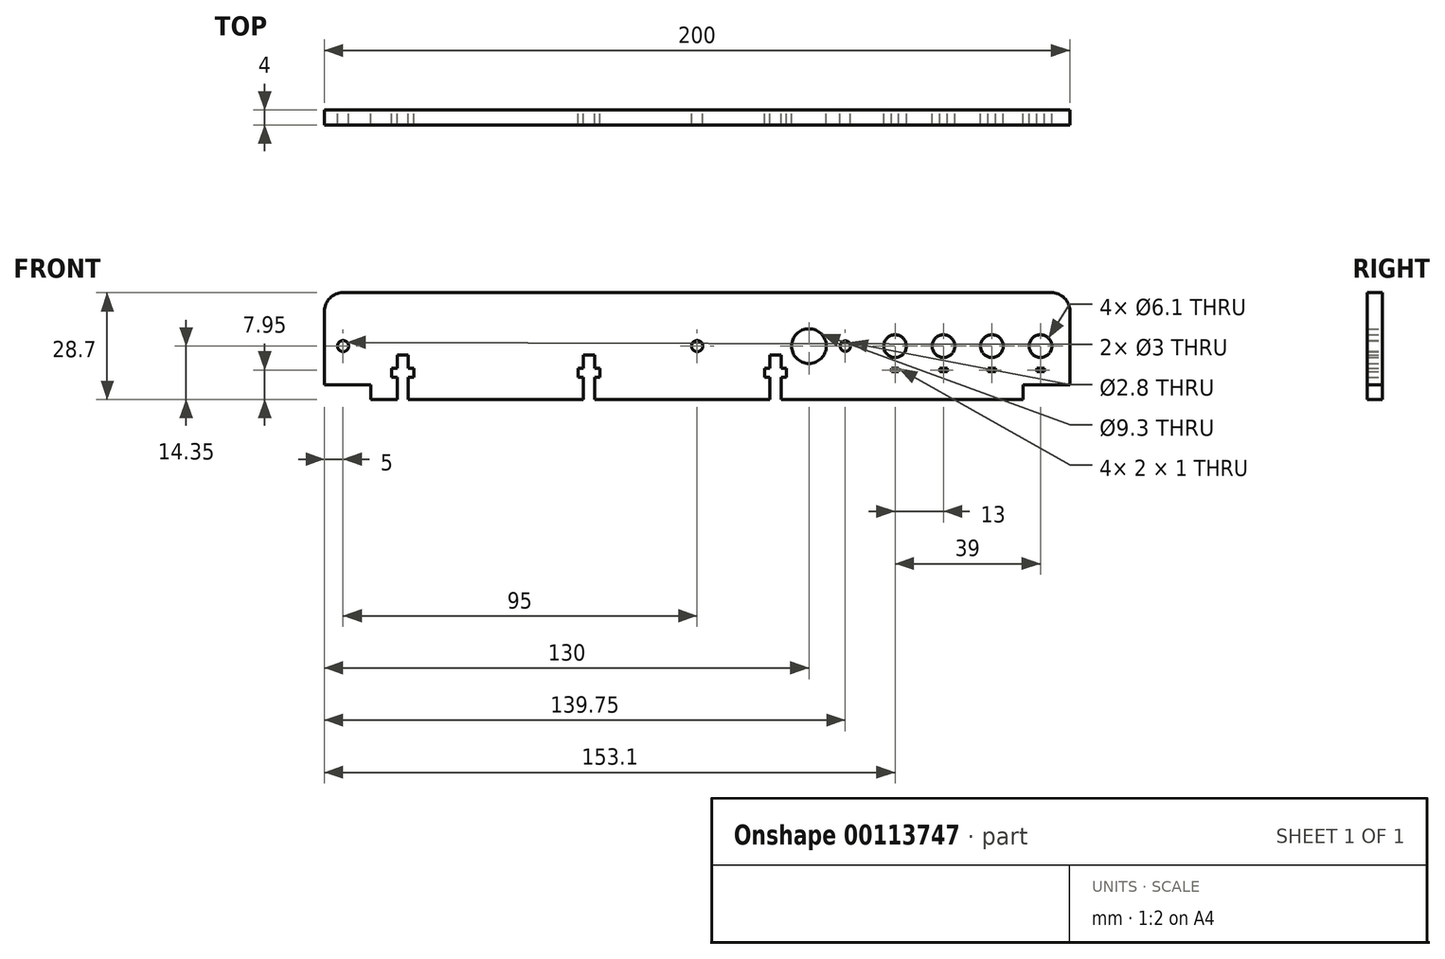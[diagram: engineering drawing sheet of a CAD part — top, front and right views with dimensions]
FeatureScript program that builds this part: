
annotation { "Feature Type Name" : "Feature", "Feature Type Description" : "" }
export const myFeature = defineFeature(function(context is Context, id is Id, definition is map)
    precondition{}
    {
        {
            var Q0;
            Q0=qCreatedBy(makeId("Front.planeOp"),FACE);
            var sketch = newSketch(context, id + "F0", { "sketchPlane" : qUnion([Q0])});
            skLineSegment(sketch, "E0.bottom", {"start": v(5, 28.7) * mm, "end": v(195, 28.7) * mm});
            skLineSegment(sketch, "E0.top", {"start": v(12.5, 0) * mm, "end": v(19.5, 0) * mm});
            skLineSegment(sketch, "E0.left", {"start": v(0, 23.7) * mm, "end": v(0, 4) * mm});
            skLineSegment(sketch, "E0.right", {"start": v(200, 23.7) * mm, "end": v(200, 4) * mm});
            skCircle(sketch, "E1", {"center": v(130, 14.35) * mm, "radius": 4.65 * mm});
            skCircle(sketch, "E2", {"center": v(139.75, 14.35) * mm, "radius": 1.4 * mm});
            skLineSegment(sketch, "E3", {"start": v(0, 14.35) * mm, "end": v(200, 14.35) * mm, "construction": true});
            skLineSegment(sketch, "E4.top", {"start": v(0, 4) * mm, "end": v(12.5, 4) * mm});
            skLineSegment(sketch, "E4.right", {"start": v(12.5, 0) * mm, "end": v(12.5, 4) * mm});
            skLineSegment(sketch, "E5", {"start": v(100, 28.7) * mm, "end": v(100, 0) * mm, "construction": true});
            skPoint(sketch, "E6.orphan", {"position": v(0, 0) * mm});
            skLineSegment(sketch, "E7.MirrorCS", {"start": v(187.5, 0) * mm, "end": v(187.5, 4) * mm});
            skLineSegment(sketch, "E8.MirrorCS", {"start": v(200, 4) * mm, "end": v(187.5, 4) * mm});
            skPoint(sketch, "E9.orphan", {"position": v(200, 0) * mm});
            skPoint(sketch, "E10.visualSharp", {"position": v(0, 28.7) * mm});
            skArc(sketch, "E10.filletArc", {"start": v(5, 28.7) * mm, "mid": v(1.46, 27.24) * mm, "end": v(0, 23.7) * mm});
            skPoint(sketch, "E11.visualSharp", {"position": v(200, 28.7) * mm});
            skArc(sketch, "E11.filletArc", {"start": v(200, 23.7) * mm, "mid": v(198.54, 27.24) * mm, "end": v(195, 28.7) * mm});
            skCircle(sketch, "E12", {"center": v(192.1, 14.35) * mm, "radius": 3.05 * mm});
            skCircle(sketch, "E13", {"center": v(192.1, 14.35) * mm, "radius": 5.9 * mm, "construction": true});
            skLineSegment(sketch, "E14", {"start": v(192.1, 14.35) * mm, "end": v(192.1, 4) * mm, "construction": true});
            skLineSegment(sketch, "E15.bottom", {"start": v(193.1, 7.45) * mm, "end": v(191.1, 7.45) * mm});
            skLineSegment(sketch, "E15.top", {"start": v(193.1, 8.45) * mm, "end": v(191.1, 8.45) * mm});
            skLineSegment(sketch, "E15.left", {"start": v(193.1, 7.45) * mm, "end": v(193.1, 8.45) * mm});
            skLineSegment(sketch, "E15.right", {"start": v(191.1, 7.45) * mm, "end": v(191.1, 8.45) * mm});
            skPoint(sketch, "E15.middle", {"position": v(192.1, 7.95) * mm});
            skCircle(sketch, "E16.1.0.0", {"center": v(179.1, 14.35) * mm, "radius": 3.05 * mm});
            skLineSegment(sketch, "E16.1.0.1", {"start": v(180.1, 7.45) * mm, "end": v(180.1, 8.45) * mm});
            skLineSegment(sketch, "E16.1.0.2", {"start": v(180.1, 8.45) * mm, "end": v(178.1, 8.45) * mm});
            skLineSegment(sketch, "E16.1.0.3", {"start": v(178.1, 7.45) * mm, "end": v(178.1, 8.45) * mm});
            skLineSegment(sketch, "E16.1.0.4", {"start": v(180.1, 7.45) * mm, "end": v(178.1, 7.45) * mm});
            skCircle(sketch, "E16.1.0.5", {"center": v(179.1, 14.35) * mm, "radius": 5.9 * mm, "construction": true});
            skCircle(sketch, "E16.2.0.0", {"center": v(166.1, 14.35) * mm, "radius": 3.05 * mm});
            skLineSegment(sketch, "E16.2.0.1", {"start": v(167.1, 7.45) * mm, "end": v(167.1, 8.45) * mm});
            skLineSegment(sketch, "E16.2.0.2", {"start": v(167.1, 8.45) * mm, "end": v(165.1, 8.45) * mm});
            skLineSegment(sketch, "E16.2.0.3", {"start": v(165.1, 7.45) * mm, "end": v(165.1, 8.45) * mm});
            skLineSegment(sketch, "E16.2.0.4", {"start": v(167.1, 7.45) * mm, "end": v(165.1, 7.45) * mm});
            skCircle(sketch, "E16.2.0.5", {"center": v(166.1, 14.35) * mm, "radius": 5.9 * mm, "construction": true});
            skLineSegment(sketch, "E16.direction1", {"start": v(191.1, 7.45) * mm, "end": v(178.1, 7.45) * mm, "construction": true});
            skLineSegment(sketch, "E17.top", {"start": v(19.5, 12) * mm, "end": v(22.5, 12) * mm});
            skLineSegment(sketch, "E17.left", {"start": v(19.5, 0) * mm, "end": v(19.5, 6) * mm});
            skLineSegment(sketch, "E17.right", {"start": v(22.5, 0) * mm, "end": v(22.5, 6) * mm});
            skCircle(sketch, "E18", {"center": v(5, 14.35) * mm, "radius": 1.5 * mm});
            skCircle(sketch, "E19", {"center": v(100, 14.35) * mm, "radius": 1.5 * mm});
            skPoint(sketch, "E20.oppositeSnap0", {"position": v(22.5, 6) * mm});
            skLineSegment(sketch, "E20.bottom", {"start": v(18.05, 8.4) * mm, "end": v(19.5, 8.4) * mm});
            skLineSegment(sketch, "E20.top", {"start": v(18.05, 6) * mm, "end": v(19.5, 6) * mm});
            skLineSegment(sketch, "E20.left", {"start": v(18.05, 8.4) * mm, "end": v(18.05, 6) * mm});
            skLineSegment(sketch, "E20.right", {"start": v(23.95, 8.4) * mm, "end": v(23.95, 6) * mm});
            skLineSegment(sketch, "E21", {"start": v(21, 12) * mm, "end": v(21, 0) * mm, "construction": true});
            skLineSegment(sketch, "E22.trimOffspring", {"start": v(22.5, 0) * mm, "end": v(69.5, 0) * mm});
            skLineSegment(sketch, "E23", {"start": v(21, 8.4) * mm, "end": v(21, 6) * mm, "construction": true});
            skLineSegment(sketch, "E24.trimOffspring", {"start": v(22.5, 8.4) * mm, "end": v(22.5, 12) * mm});
            skLineSegment(sketch, "E25.trimOffspring", {"start": v(19.5, 8.4) * mm, "end": v(19.5, 12) * mm});
            skLineSegment(sketch, "E26.trimOffspring", {"start": v(22.5, 8.4) * mm, "end": v(23.95, 8.4) * mm});
            skLineSegment(sketch, "E27.trimOffspring", {"start": v(22.5, 6) * mm, "end": v(23.95, 6) * mm});
            skLineSegment(sketch, "E28.1.0.0", {"start": v(68.05, 8.4) * mm, "end": v(68.05, 6) * mm});
            skPoint(sketch, "E28.1.0.1", {"position": v(72.5, 6) * mm});
            skLineSegment(sketch, "E28.1.0.2", {"start": v(69.5, 12) * mm, "end": v(72.5, 12) * mm});
            skLineSegment(sketch, "E28.1.0.3", {"start": v(68.05, 6) * mm, "end": v(69.5, 6) * mm});
            skLineSegment(sketch, "E28.1.0.4", {"start": v(72.5, 6) * mm, "end": v(73.95, 6) * mm});
            skLineSegment(sketch, "E28.1.0.5", {"start": v(69.5, 8.4) * mm, "end": v(69.5, 12) * mm});
            skLineSegment(sketch, "E28.1.0.6", {"start": v(68.05, 8.4) * mm, "end": v(69.5, 8.4) * mm});
            skLineSegment(sketch, "E28.1.0.7", {"start": v(73.95, 8.4) * mm, "end": v(73.95, 6) * mm});
            skLineSegment(sketch, "E28.1.0.8", {"start": v(72.5, 8.4) * mm, "end": v(73.95, 8.4) * mm});
            skLineSegment(sketch, "E28.1.0.9", {"start": v(72.5, 8.4) * mm, "end": v(72.5, 12) * mm});
            skLineSegment(sketch, "E28.1.0.10", {"start": v(72.5, 0) * mm, "end": v(72.5, 6) * mm});
            skLineSegment(sketch, "E28.1.0.11", {"start": v(69.5, 0) * mm, "end": v(69.5, 6) * mm});
            skLineSegment(sketch, "E28.2.0.0", {"start": v(118.05, 8.4) * mm, "end": v(118.05, 6) * mm});
            skPoint(sketch, "E28.2.0.1", {"position": v(122.5, 6) * mm});
            skLineSegment(sketch, "E28.2.0.2", {"start": v(119.5, 12) * mm, "end": v(122.5, 12) * mm});
            skLineSegment(sketch, "E28.2.0.3", {"start": v(118.05, 6) * mm, "end": v(119.5, 6) * mm});
            skLineSegment(sketch, "E28.2.0.4", {"start": v(122.5, 6) * mm, "end": v(123.95, 6) * mm});
            skLineSegment(sketch, "E28.2.0.5", {"start": v(119.5, 8.4) * mm, "end": v(119.5, 12) * mm});
            skLineSegment(sketch, "E28.2.0.6", {"start": v(118.05, 8.4) * mm, "end": v(119.5, 8.4) * mm});
            skLineSegment(sketch, "E28.2.0.7", {"start": v(123.95, 8.4) * mm, "end": v(123.95, 6) * mm});
            skLineSegment(sketch, "E28.2.0.8", {"start": v(122.5, 8.4) * mm, "end": v(123.95, 8.4) * mm});
            skLineSegment(sketch, "E28.2.0.9", {"start": v(122.5, 8.4) * mm, "end": v(122.5, 12) * mm});
            skLineSegment(sketch, "E28.2.0.10", {"start": v(122.5, 0) * mm, "end": v(122.5, 6) * mm});
            skLineSegment(sketch, "E28.2.0.11", {"start": v(119.5, 0) * mm, "end": v(119.5, 6) * mm});
            skLineSegment(sketch, "E28.direction1", {"start": v(18.05, 6) * mm, "end": v(68.05, 6) * mm, "construction": true});
            skLineSegment(sketch, "E29.trimOffspring", {"start": v(72.5, 0) * mm, "end": v(119.5, 0) * mm});
            skLineSegment(sketch, "E30.trimOffspring", {"start": v(122.5, 0) * mm, "end": v(187.5, 0) * mm});
            skCircle(sketch, "E31.0.3.0", {"center": v(153.1, 14.35) * mm, "radius": 3.05 * mm});
            skLineSegment(sketch, "E31.2.3.0", {"start": v(154.1, 7.45) * mm, "end": v(154.1, 8.45) * mm});
            skLineSegment(sketch, "E31.5.3.0", {"start": v(154.1, 8.45) * mm, "end": v(152.1, 8.45) * mm});
            skLineSegment(sketch, "E31.8.3.0", {"start": v(152.1, 7.45) * mm, "end": v(152.1, 8.45) * mm});
            skLineSegment(sketch, "E31.11.3.0", {"start": v(154.1, 7.45) * mm, "end": v(152.1, 7.45) * mm});
            skCircle(sketch, "E31.14.3.0", {"center": v(153.1, 14.35) * mm, "radius": 5.9 * mm, "construction": true});
            skSolve(sketch);
        }
        {
            var Q0;
            Q0 = qSketchRegion(id + "F0", true);
            extrude(context, id + "F1", {"entities" : qUnion([Q0]), "depth" : 4 * mm});
        }
    });
